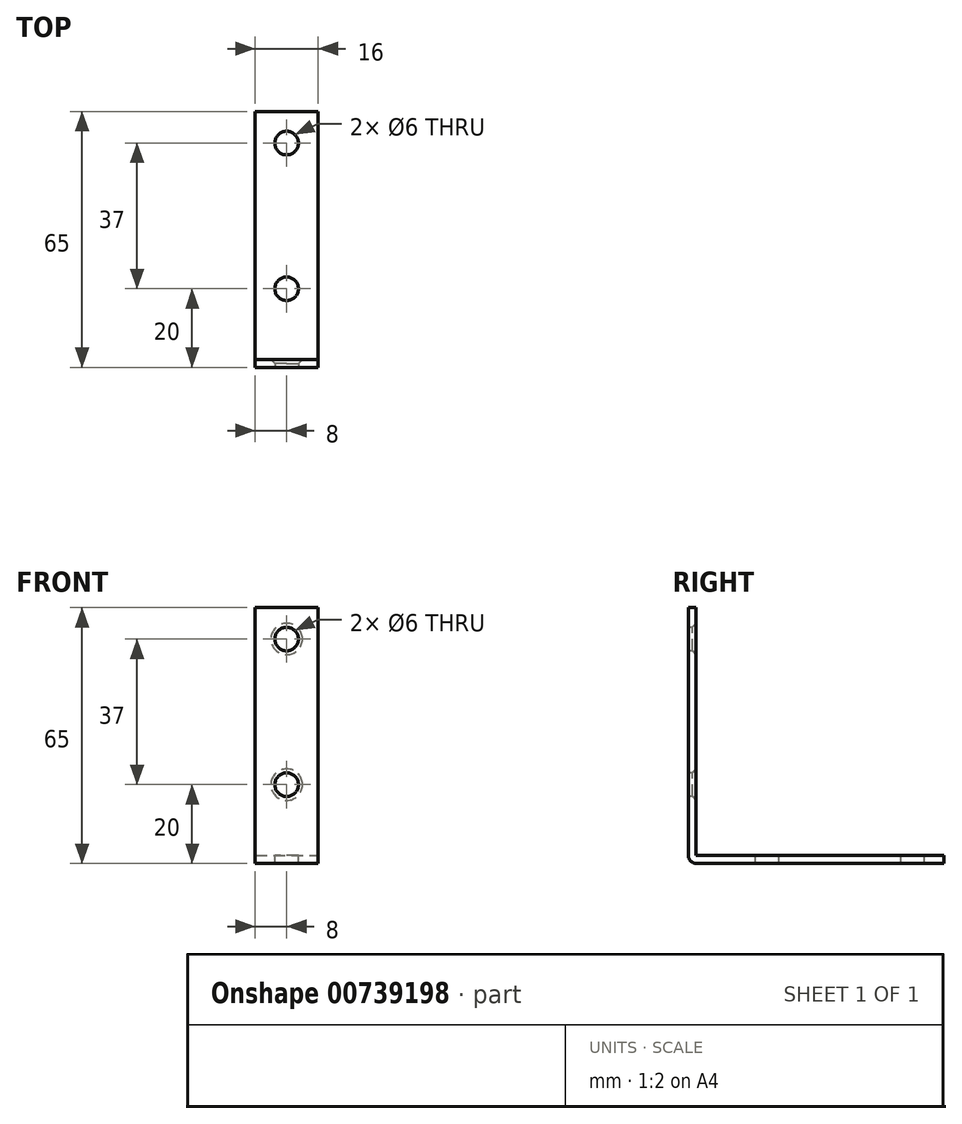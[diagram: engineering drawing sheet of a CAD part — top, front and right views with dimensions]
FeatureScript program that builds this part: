
annotation { "Feature Type Name" : "Feature", "Feature Type Description" : "" }
export const myFeature = defineFeature(function(context is Context, id is Id, definition is map)
    precondition{}
    {
        {
            var Q0;
            Q0=qCreatedBy(makeId("Top.planeOp"),FACE);
            var sketch = newSketch(context, id + "F0", { "sketchPlane" : qUnion([Q0])});
            skLineSegment(sketch, "E0.bottom", {"start": v(0, 0) * mm, "end": v(16, 0) * mm});
            skLineSegment(sketch, "E0.top", {"start": v(0, 65) * mm, "end": v(16, 65) * mm});
            skLineSegment(sketch, "E0.left", {"start": v(0, 0) * mm, "end": v(0, 65) * mm});
            skLineSegment(sketch, "E0.right", {"start": v(16, 0) * mm, "end": v(16, 65) * mm});
            skSolve(sketch);
        }
        {
            var Q0;
            Q0 = qSketchRegion(id + "F0", true);
            extrude(context, id + "F1", {"entities" : qUnion([Q0]), "depth" : 2 * mm, "offsetDistance" : 25 * mm});
        }
        {
            var Q0;
            Q0=makeQuery(id+"F1.opExtrude","CAP_FACE",FACE,{"disambiguationData":[OSD([sQuery(id+"F0.wireOp",EDGE,"E0.bottom"),sQuery(id+"F0.wireOp",EDGE,"E0.top"),sQuery(id+"F0.wireOp",EDGE,"E0.left"),sQuery(id+"F0.wireOp",EDGE,"E0.right")])],"isStart":false});
            var sketch = newSketch(context, id + "F2", { "sketchPlane" : qUnion([Q0])});
            skLineSegment(sketch, "E1.bottom", {"start": v(0, 0) * mm, "end": v(16, 0) * mm});
            skLineSegment(sketch, "E1.top", {"start": v(0, 2) * mm, "end": v(16, 2) * mm});
            skLineSegment(sketch, "E1.left", {"start": v(0, 0) * mm, "end": v(0, 2) * mm});
            skLineSegment(sketch, "E1.right", {"start": v(16, 0) * mm, "end": v(16, 2) * mm});
            skSolve(sketch);
        }
        {
            var Q0;
            Q0 = qSketchRegion(id + "F2", true);
            extrude(context, id + "F3", {"entities" : qUnion([Q0]), "operationType" : NewBodyOperationType.ADD, "depth" : 63 * mm, "offsetDistance" : 25 * mm});
        }
        {
            var Q0;
            Q0=makeQuery(id+"F1.opExtrude","CAP_FACE",FACE,{"disambiguationData":[OSD([sQuery(id+"F0.wireOp",EDGE,"E0.bottom"),sQuery(id+"F0.wireOp",EDGE,"E0.top"),sQuery(id+"F0.wireOp",EDGE,"E0.left"),sQuery(id+"F0.wireOp",EDGE,"E0.right")])],"isStart":false});
            var sketch = newSketch(context, id + "F4", { "sketchPlane" : qUnion([Q0])});
            skCircle(sketch, "E2", {"center": v(8, 57) * mm, "radius": 3 * mm});
            skPoint(sketch, "E2.centerSnap0", {"position": v(8, 65) * mm});
            skCircle(sketch, "E3", {"center": v(8, 20) * mm, "radius": 3 * mm});
            skSolve(sketch);
        }
        {
            var Q0;
            Q0 = qSketchRegion(id + "F4", true);
            extrude(context, id + "F5", {"entities" : qUnion([Q0]), "operationType" : NewBodyOperationType.REMOVE, "endBound" : BoundingType.THROUGH_ALL, "oppositeDirection" : true, "depth" : 25 * mm, "offsetDistance" : 25 * mm});
        }
        {
            var Q0;
            Q0=makeQuery(id+"F3.boolean.opBoolean","MERGE",FACE,{"derivedFrom":[makeQuery(id+"F1.opExtrude","SWEPT_FACE",FACE,{"disambiguationData":[OSD([sQuery(id+"F0.wireOp",EDGE,"E0.bottom")])]}),makeQuery(id+"F3.opExtrude","SWEPT_FACE",FACE,{"disambiguationData":[OSD([sQuery(id+"F2.wireOp",EDGE,"E1.bottom")])]})]});
            var sketch = newSketch(context, id + "F6", { "sketchPlane" : qUnion([Q0])});
            skCircle(sketch, "E4", {"center": v(8, 57) * mm, "radius": 3 * mm});
            skPoint(sketch, "E4.centerSnap0", {"position": v(8, 65) * mm});
            skCircle(sketch, "E5", {"center": v(8, 20) * mm, "radius": 3 * mm});
            skSolve(sketch);
        }
        {
            var Q0;
            Q0 = qSketchRegion(id + "F6", true);
            extrude(context, id + "F7", {"entities" : qUnion([Q0]), "operationType" : NewBodyOperationType.REMOVE, "endBound" : BoundingType.THROUGH_ALL, "oppositeDirection" : true, "depth" : 25 * mm, "offsetDistance" : 25 * mm});
        }
        {
            var Q0;
            Q0=makeQuery(id+"F7.boolean.opBoolean","INTERSECT",EDGE,{"derivedFrom":[makeQuery(id+"F3.opExtrude","SWEPT_FACE",FACE,{"disambiguationData":[OSD([sQuery(id+"F2.wireOp",EDGE,"E1.top")])]}),makeQuery(id+"F7.opExtrude","SWEPT_FACE",FACE,{"disambiguationData":[OSD([sQuery(id+"F6.wireOp",EDGE,"E4")])]})]});
            var Q1;
            Q1=makeQuery(id+"F7.boolean.opBoolean","INTERSECT",EDGE,{"derivedFrom":[makeQuery(id+"F3.opExtrude","SWEPT_FACE",FACE,{"disambiguationData":[OSD([sQuery(id+"F2.wireOp",EDGE,"E1.top")])]}),makeQuery(id+"F7.opExtrude","SWEPT_FACE",FACE,{"disambiguationData":[OSD([sQuery(id+"F6.wireOp",EDGE,"E5")])]})]});
            var Q2;
            Q2=makeQuery(id+"F5.boolean.opBoolean","COPY",EDGE,{"derivedFrom":makeQuery(id+"F5.opExtrude","CAP_EDGE",EDGE,{"disambiguationData":[OSD([sQuery(id+"F4.wireOp",EDGE,"E3")])],"isStart":true})});
            var Q3;
            Q3=makeQuery(id+"F5.boolean.opBoolean","COPY",EDGE,{"derivedFrom":makeQuery(id+"F5.opExtrude","CAP_EDGE",EDGE,{"disambiguationData":[OSD([sQuery(id+"F4.wireOp",EDGE,"E2")])],"isStart":true})});
            chamfer(context, id + "F8", {"entities" : qUnion([Q0, Q1, Q2, Q3]), "width" : 1 * mm, "tangentPropagation" : true});
        }
        {
            var Q0;
            Q0=makeQuery(id+"F1.opExtrude","CAP_EDGE",EDGE,{"disambiguationData":[OSD([sQuery(id+"F0.wireOp",EDGE,"E0.bottom")])],"isStart":true});
            fillet(context, id + "F9", {"entities" : qUnion([Q0]), "radius" : 2 * mm, "tangentPropagation" : true, "allowEdgeOverflow" : false});
        }
    });
